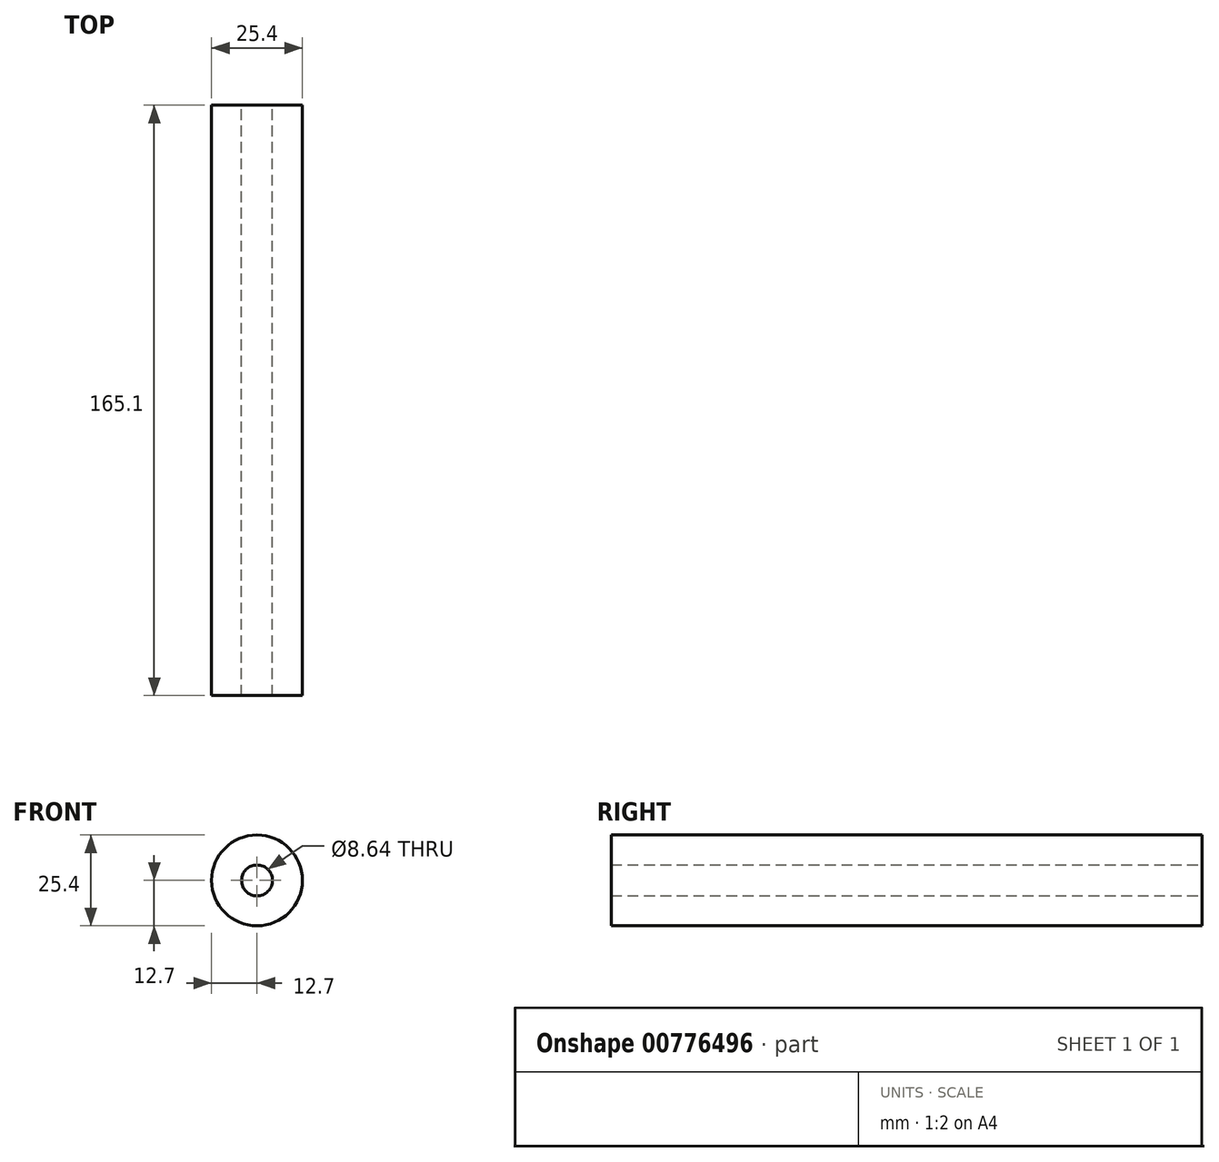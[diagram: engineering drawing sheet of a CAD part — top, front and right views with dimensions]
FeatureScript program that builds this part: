
annotation { "Feature Type Name" : "Feature", "Feature Type Description" : "" }
export const myFeature = defineFeature(function(context is Context, id is Id, definition is map)
    precondition{}
    {
        {
            var Q0;
            Q0=qCreatedBy(makeId("Front.planeOp"),FACE);
            var sketch = newSketch(context, id + "F0", { "sketchPlane" : qUnion([Q0])});
            skCircle(sketch, "E0", {"center": v(0, 0) * mm, "radius": 4.32 * mm});
            skCircle(sketch, "E1", {"center": v(0, 0) * mm, "radius": 12.7 * mm});
            skSolve(sketch);
        }
        {
            var Q0;
            Q0=qSketchRegion(id+"F0",true);
            extrude(context, id + "F1", {"entities" : qUnion([Q0]), "depth" : 165.1 * mm, "offsetDistance" : 25.4 * mm});
        }
    });
